FCSTD DOCUMENT  (FreeCAD 1.0R39109 (Git))
Label: Setup transmission
License: All rights reserved
LicenseURL: https://en.wikipedia.org/wiki/All_rights_reserved
objects: App::Link×30, PartDesign::CoordinateSystem×15, Part::FeaturePython×12, App::DocumentObjectGroup×2, App::FeaturePython×1, App::Part×1
note: 27 computed .brp shape members not serialized (recipe doc carries the construction recipe); baked Part::Feature solids carry a one-line shape summary decoded from their .brp
EXTERNAL_REF file=Optomecanics/Optical_table.FCStd obj=HoleAxis_1
EXTERNAL_REF file=Optomecanics/Optical_table.FCStd obj=Assembly
EXTERNAL_REF file=Cryostat/Cryo_sketch.FCStd obj=LCS_Origin
EXTERNAL_REF file=Cryostat/Cryo_sketch.FCStd obj=Assembly
EXTERNAL_REF file=Cryostat/Cryo_sketch.FCStd obj=Sample_position
EXTERNAL_REF file=Samples/Sample.FCStd obj=LCS_Origin
EXTERNAL_REF file=Samples/Sample.FCStd obj=Assembly
EXTERNAL_REF file=Optomecanics/Mount_assembly_1inch.FCStd obj=Botto_center_minus_6
EXTERNAL_REF file=Optomecanics/Mount_assembly_1inch.FCStd obj=Assembly
EXTERNAL_REF file=Optomecanics/Mount_assembly_1inch.FCStd obj=Bottom_center_6
EXTERNAL_REF file=Optomecanics/Mount_assembly_1inch.FCStd obj=Bottom_center_minus_20
EXTERNAL_REF file=Fiber components/Fiber_mount_assembly.FCStd obj=Center_minus_6deg
EXTERNAL_REF file=Fiber components/Fiber_mount_assembly.FCStd obj=Assembly
EXTERNAL_REF file=Fiber components/Fiber_mount_assembly.FCStd obj=Center_6deg
EXTERNAL_REF file=Optics/Mirror_1inch.FCStd obj=Mirror_face_center
EXTERNAL_REF file=Optomecanics/Mount_assembly_1inch.FCStd obj=LCS_3
EXTERNAL_REF file=Optics/Mirror_1inch.FCStd obj=BB1_E03_mirror
EXTERNAL_REF file=Fiber components/Fiber_mount_assembly.FCStd obj=Center_40det
EXTERNAL_REF file=Optomecanics/Mount_assembly_2inches.FCStd obj=LCS_Origin
EXTERNAL_REF file=Optomecanics/Mount_assembly_2inches.FCStd obj=Assembly
EXTERNAL_REF file=Optomecanics/Optical_table.FCStd obj=HoleAxis_14
EXTERNAL_REF file=Optomecanics/Mount_assembly_1inch.FCStd obj=Bottom_center
EXTERNAL_REF file=Optomecanics/Optical_table.FCStd obj=HoleAxis_15
EXTERNAL_REF file=Optomecanics/Mount_assembly_1inch.FCStd obj=Bottom_center_67
EXTERNAL_REF file=Optomecanics/Optical_table.FCStd obj=HoleAxis_12
EXTERNAL_REF file=Optomecanics/Optical_table.FCStd obj=HoleAxis_6
EXTERNAL_REF file=Optics/Monochromator.FCStd obj=LCS_1
EXTERNAL_REF file=Optics/Monochromator.FCStd obj=Assembly
EXTERNAL_REF file=Optomecanics/Mount_assembly_1inch.FCStd obj=_5
EXTERNAL_REF file=Optomecanics/Optical_table.FCStd obj=HoleAxis_7
EXTERNAL_REF file=Optomecanics/Optical_table.FCStd obj=HoleAxis_2
EXTERNAL_REF file=Optomecanics/Mount_assembly_1inch.FCStd obj=LCS_Origin
EXTERNAL_REF file=Optomecanics/Optical_table.FCStd obj=HoleAxis_17
EXTERNAL_REF file=Optics/Shamrock.FCStd obj=LCS_1
EXTERNAL_REF file=Optics/Shamrock.FCStd obj=Assembly

FEATURE [PartDesign::CoordinateSystem] LCS_Origin
  AttacherType = Attacher::AttachEngine3D
  AttachmentSupport = -> [X_Axis]
  MapMode = 2
FEATURE [App::DocumentObjectGroup] Constraints
FEATURE [App::FeaturePython] Variables  # WARN: FeaturePython — macro-defined, semantics opaque (R4)
  Type = App::PropertyContainer
FEATURE [App::DocumentObjectGroup] Configurations
FEATURE [PartDesign::CoordinateSystem] COLBERT_mirror_LCS  label="COLBERT_InputLensLCS"
  AttacherType = Attacher::AttachEngine3D
  Placement = pos=(0,400,0) rot=(0,0,1;0rad)
FEATURE [PartDesign::CoordinateSystem] Input_lens_LCS  label="ReflectedLensLCS"
  AttacherType = Attacher::AttachEngine3D
  Placement = pos=(26.13,248.63,0) rot=(0,0,1;0rad)
FEATURE [PartDesign::CoordinateSystem] Output_lens_LCS  label="InputLensLCS"
  AttacherType = Attacher::AttachEngine3D
  Placement = pos=(-26.13,248.63,0) rot=(0,0,1;0rad)
FEATURE [PartDesign::CoordinateSystem] Transmitted_lens_LCS  label="TransmittedLensLCS"
  AttacherType = Attacher::AttachEngine3D
  Placement = pos=(-26.13,-248.63,0) rot=(0,0,1;0rad)
FEATURE [PartDesign::CoordinateSystem] BS_LCS  label="BSLCS"
  AttacherType = Attacher::AttachEngine3D
  Placement = pos=(31.36,298.35,0) rot=(0,0,1;0rad)
FEATURE [PartDesign::CoordinateSystem] R_col_LCS  label="ReferenceColLCS"
  AttacherType = Attacher::AttachEngine3D
  Placement = pos=(-69,400,0) rot=(0,0,1;0rad)
FEATURE [PartDesign::CoordinateSystem] Reflection_col_LCS  label="ReflectionColLCS"
  AttacherType = Attacher::AttachEngine3D
  Placement = pos=(-31.36,298.36,0) rot=(0,0,1;0rad)
FEATURE [PartDesign::CoordinateSystem] Transmission_col_LCS  label="TransmissionColLCS"
  AttacherType = Attacher::AttachEngine3D
  Placement = pos=(-32.4,-308.3,0) rot=(0,0,1;0rad)
FEATURE [Part::FeaturePython] Ray003  label="Reference_beam"  # WARN: FeaturePython — macro-defined, semantics opaque (R4)
  BeamDistance = 0.1
  BeamNrColumns = 1
  BeamNrRows = 1
  ConeAngle = 360
  FocalPoint = (0,0,100)
  HideFirstPart = false
  MaxNrReflections = 200
  MaxRayLength = 170
  Order = 0
  Placement = pos=(41.81,397.81,199.9) rot=(0,0,-1;1.67552rad)
  Power = true
  RayBundleType = 0
  Spherical = false
  Wavelength = 580
FEATURE [App::Link] Optical_table
  AttachedBy = #HoleAxis_1
  AttachedTo = Parent Assembly#LCS_Origin
  LinkPlacement = pos=(546.1,-850.9,-110) rot=(0.57735,0.57735,0.57735;2.0944rad)
  LinkedObject = -> <external Optomecanics/Optical_table.FCStd>#Assembly
  Placement = pos=(546.1,-850.9,-110) rot=(0.57735,0.57735,0.57735;2.0944rad)
  SolverId = Asm4EE
  expr: Placement = LCS_Origin.Placement * AttachmentOffset * Optical_table#HoleAxis_1.Placement ^ -1
FEATURE [App::Link] Cryo
  AttachedBy = #LCS_Origin
  AttachedTo = Optical_table#HoleAxis_1
  LinkPlacement = pos=(-1.137e-13,1.137e-13,-1.279e-13) rot=(0,0,1;0rad)
  LinkedObject = -> <external Cryostat/Cryo_sketch.FCStd>#Assembly
  Placement = pos=(-1.137e-13,1.137e-13,-1.279e-13) rot=(0,0,1;0rad)
  SolverId = Asm4EE
  expr: Placement = Optical_table.Placement * Optical_table#HoleAxis_1.Placement * AttachmentOffset * Cryo_sketch#LCS_Origin.Placement ^ -1
FEATURE [App::Link] Sample
  AttachedBy = #LCS_Origin
  AttachedTo = Cryo#Sample_position
  LinkPlacement = pos=(-1.336e-13,1.236e-13,179.46) rot=(0,0,1;3.14159rad)
  LinkedObject = -> <external Samples/Sample.FCStd>#Assembly
  Placement = pos=(-1.336e-13,1.236e-13,179.46) rot=(0,0,1;3.14159rad)
  SolverId = Asm4EE
  expr: Placement = Cryo.Placement * Cryo_sketch#Sample_position.Placement * AttachmentOffset * Sample#LCS_Origin.Placement ^ -1
FEATURE [App::Link] Mount_assembly_1inch  label="InputLensMount"
  AttachedBy = #Botto_center_minus_6
  AttachedTo = Parent Assembly#Output_lens_LCS
  AttachmentOffset = pos=(0,0,0) rot=(0,0,1;1.5708rad)
  LinkPlacement = pos=(-26.13,248.63,0) rot=(0,0,1;1.67552rad)
  LinkedObject = -> <external Optomecanics/Mount_assembly_1inch.FCStd>#Assembly
  Placement = pos=(-26.13,248.63,0) rot=(0,0,1;1.67552rad)
  SolverId = Asm4EE
  expr: Placement = Output_lens_LCS.Placement * AttachmentOffset * Mount_assembly_1inch#Botto_center_minus_6.Placement ^ -1
FEATURE [App::Link] InputLensMount  label="ReflectedLensMount"
  AttachedBy = #Bottom_center_6
  AttachedTo = Parent Assembly#Input_lens_LCS
  AttachmentOffset = pos=(0,0,0) rot=(0,0,1;1.5708rad)
  LinkPlacement = pos=(26.13,248.63,0) rot=(0,0,1;1.46608rad)
  LinkedObject = -> <external Optomecanics/Mount_assembly_1inch.FCStd>#Assembly
  Placement = pos=(26.13,248.63,0) rot=(0,0,1;1.46608rad)
  SolverId = Asm4EE
  expr: Placement = Input_lens_LCS.Placement * AttachmentOffset * Mount_assembly_1inch#Bottom_center_6.Placement ^ -1
FEATURE [App::Link] Mount_assembly_1inch001  label="TransmittedLensMount"
  AttachedBy = #Botto_center_minus_6
  AttachedTo = Parent Assembly#Transmitted_lens_LCS
  AttachmentOffset = pos=(0,0,0) rot=(0,0,1;1.5708rad)
  LinkPlacement = pos=(-26.13,-248.63,0) rot=(0,0,1;1.67552rad)
  LinkedObject = -> <external Optomecanics/Mount_assembly_1inch.FCStd>#Assembly
  Placement = pos=(-26.13,-248.63,0) rot=(0,0,1;1.67552rad)
  SolverId = Asm4EE
  expr: Placement = Transmitted_lens_LCS.Placement * AttachmentOffset * Mount_assembly_1inch#Botto_center_minus_6.Placement ^ -1
FEATURE [App::Link] Mount_assembly_1inch002  label="BSMount"
  AttachedBy = #Bottom_center_minus_20
  AttachedTo = Parent Assembly#BS_LCS
  AttachmentOffset = pos=(0,0,0) rot=(0,0,1;4.71239rad)
  LinkPlacement = pos=(31.36,298.35,0) rot=(0,0,1;5.06145rad)
  LinkedObject = -> <external Optomecanics/Mount_assembly_1inch.FCStd>#Assembly
  Placement = pos=(31.36,298.35,0) rot=(0,0,1;5.06145rad)
  SolverId = Asm4EE
  expr: Placement = BS_LCS.Placement * AttachmentOffset * Mount_assembly_1inch#Bottom_center_minus_20.Placement ^ -1
FEATURE [App::Link] Fiber_mount_assembly  label="ReflectedFiberCol"
  AttachedBy = #Center_minus_6deg
  AttachedTo = Parent Assembly#Reflection_col_LCS
  AttachmentOffset = pos=(0,0,0) rot=(0,0,1;1.5708rad)
  LinkPlacement = pos=(-31.36,298.36,0) rot=(0,0,1;1.67552rad)
  LinkedObject = -> <external Fiber components/Fiber_mount_assembly.FCStd>#Assembly
  Placement = pos=(-31.36,298.36,0) rot=(0,0,1;1.67552rad)
  SolverId = Asm4EE
  expr: Placement = Reflection_col_LCS.Placement * AttachmentOffset * Fiber_mount_assembly#Center_minus_6deg.Placement ^ -1
FEATURE [App::Link] ReflectedFiberCol  label="TransmittedFiberCol"
  AttachedBy = #Center_6deg
  AttachedTo = Parent Assembly#Transmission_col_LCS
  AttachmentOffset = pos=(0,0,0) rot=(0,0,1;4.71239rad)
  LinkPlacement = pos=(-32.4,-308.3,0) rot=(0,0,1;4.60767rad)
  LinkedObject = -> <external Fiber components/Fiber_mount_assembly.FCStd>#Assembly
  Placement = pos=(-32.4,-308.3,0) rot=(0,0,1;4.60767rad)
  SolverId = Asm4EE
  expr: Placement = Transmission_col_LCS.Placement * AttachmentOffset * Fiber_mount_assembly#Center_6deg.Placement ^ -1
FEATURE [App::Link] BB1_E03_mirror  label="BS(Actually_a_mirror)"
  AttachedBy = #Mirror_face_center
  AttachedTo = Mount_assembly_1inch002#LCS_3
  AttachmentOffset = pos=(-4,0,0) rot=(0,0.707107,0.707107;3.14159rad)
  LinkPlacement = pos=(-5.01782,297.683,189.089) rot=(0,0,-1;2.79253rad)
  LinkedObject = -> <external Optics/Mirror_1inch.FCStd>#BB1_E03_mirror
  Placement = pos=(-5.01782,297.683,189.089) rot=(0,0,-1;2.79253rad)
  SolverId = Asm4EE
  expr: Placement = Mount_assembly_1inch002.Placement * Mount_assembly_1inch#LCS_3.Placement * AttachmentOffset * Mirror_1inch#Mirror_face_center.Placement ^ -1
FEATURE [Part::FeaturePython] Mirror  label="BS_Reflectance"  # WARN: FeaturePython — macro-defined, semantics opaque (R4)
  Base = -> [BB1_E03_mirror]
  OpticalType = 0
  Transparency = 0
  collectStatistics = false
FEATURE [Part::FeaturePython] Ray  label="Reflected_beam"  # WARN: FeaturePython — macro-defined, semantics opaque (R4)
  BeamDistance = 0.1
  BeamNrColumns = 1
  BeamNrRows = 1
  ConeAngle = 380
  FocalPoint = (0,0,100)
  HideFirstPart = false
  IgnoredOpticalElements = -> [Mirror]
  MaxNrReflections = 200
  MaxRayLength = 360
  Order = 0
  Placement = pos=(31.36,298.36,199.9) rot=(0,0,-1;1.67552rad)
  Power = true
  RayBundleType = 0
  Spherical = false
  Wavelength = 580
FEATURE [Part::FeaturePython] Mirror001  label="Sample_Reflectance"  # WARN: FeaturePython — macro-defined, semantics opaque (R4)
  Base = -> [Sample]
  OpticalType = 0
  Transparency = 0
  collectStatistics = false
FEATURE [Part::FeaturePython] Ray004  label="Transmitted_beam"  # WARN: FeaturePython — macro-defined, semantics opaque (R4)
  BeamDistance = 0.1
  BeamNrColumns = 1
  BeamNrRows = 1
  ConeAngle = 360
  FocalPoint = (0,0,100)
  HideFirstPart = false
  IgnoredOpticalElements = -> [Mirror,Mirror001]
  MaxNrReflections = 200
  MaxRayLength = 755
  Order = 0
  Placement = pos=(41.81,398.81,199.9) rot=(0,0,-1;1.67552rad)
  Power = true
  RayBundleType = 0
  Spherical = false
  Wavelength = 580
FEATURE [Part::FeaturePython] Ray005  label="COLBERT_beam"  # WARN: FeaturePython — macro-defined, semantics opaque (R4)
  BeamDistance = 12.7
  BeamNrColumns = 2
  BeamNrRows = 2
  ConeAngle = 360
  FocalPoint = (0,0,100)
  HideFirstPart = false
  IgnoredOpticalElements = -> [Mirror001]
  MaxNrReflections = 200
  MaxRayLength = 2000
  Order = 0
  Placement = pos=(-6.35,700,193.55) rot=(0,0,-1;1.5708rad)
  Power = true
  RayBundleType = 0
  Spherical = false
  Wavelength = 580
FEATURE [App::Link] Fiber_mount_assembly001  label="ReferenceFiberCol"
  AttachedBy = #Center_40det
  AttachedTo = Parent Assembly#R_col_LCS
  AttachmentOffset = pos=(0,0,0) rot=(0,0,1;3.14159rad)
  LinkPlacement = pos=(-69,400,0) rot=(0,0,1;2.3911rad)
  LinkedObject = -> <external Fiber components/Fiber_mount_assembly.FCStd>#Assembly
  Placement = pos=(-69,400,0) rot=(0,0,1;2.3911rad)
  SolverId = Asm4EE
  expr: Placement = R_col_LCS.Placement * AttachmentOffset * Fiber_mount_assembly#Center_40det.Placement ^ -1
FEATURE [App::Link] Mount_assembly_2inches  label="InputLensMountCOLBERT"
  AttachedBy = #LCS_Origin
  AttachedTo = Parent Assembly#COLBERT_mirror_LCS
  AttachmentOffset = pos=(0,100,0) rot=(0,0,1;1.5708rad)
  LinkPlacement = pos=(0,500,0) rot=(0,0,1;1.5708rad)
  LinkedObject = -> <external Optomecanics/Mount_assembly_2inches.FCStd>#Assembly
  Placement = pos=(0,500,0) rot=(0,0,1;1.5708rad)
  SolverId = Asm4EE
  expr: Placement = COLBERT_mirror_LCS.Placement * AttachmentOffset * Mount_assembly_2inches#LCS_Origin.Placement ^ -1
FEATURE [App::Link] Mount_assembly_2inches_2  label="OutputLensMountCOLBERT"
  AttachedBy = #LCS_Origin
  AttachedTo = Optical_table#HoleAxis_14
  AttachmentOffset = pos=(0,0,0) rot=(0,0,1;1.5708rad)
  LinkPlacement = pos=(-2.274e-13,-508,-9.95e-14) rot=(0,0,1;1.5708rad)
  LinkedObject = -> <external Optomecanics/Mount_assembly_2inches.FCStd>#Assembly
  Placement = pos=(-2.274e-13,-508,-9.95e-14) rot=(0,0,1;1.5708rad)
  SolverId = Asm4EE
  expr: Placement = Optical_table.Placement * Optical_table#HoleAxis_14.Placement * AttachmentOffset * Mount_assembly_2inches#LCS_Origin.Placement ^ -1
FEATURE [App::Link] Mount_assembly_1inch003  label="TransmissionMirror1MountCOLBERT"
  AttachedBy = #Bottom_center
  AttachedTo = Optical_table#HoleAxis_15
  AttachmentOffset = pos=(0,0,0) rot=(0,0,-1;4.71239rad)
  LinkPlacement = pos=(-3.411e-13,-609.6,-9.95e-14) rot=(0,0,-1;2.04203rad)
  LinkedObject = -> <external Optomecanics/Mount_assembly_1inch.FCStd>#Assembly
  Placement = pos=(-3.411e-13,-609.6,-9.95e-14) rot=(0,0,-1;2.04203rad)
  SolverId = Asm4EE
  expr: Placement = Optical_table.Placement * Optical_table#HoleAxis_15.Placement * AttachmentOffset * Mount_assembly_1inch#Bottom_center.Placement ^ -1
FEATURE [App::Link] Mount_assembly_1inch004  label="TransmissionMirror2MountCOLBERT"
  AttachedBy = #Bottom_center_67
  AttachedTo = Optical_table#HoleAxis_12
  AttachmentOffset = pos=(25.4,0,0) rot=(0,0,-1;1.5708rad)
  LinkPlacement = pos=(203.2,-457.2,-9.67e-14) rot=(0,0,-1;2.82743rad)
  LinkedObject = -> <external Optomecanics/Mount_assembly_1inch.FCStd>#Assembly
  Placement = pos=(203.2,-457.2,-9.67e-14) rot=(0,0,-1;2.82743rad)
  SolverId = Asm4EE
  expr: Placement = Optical_table.Placement * Optical_table#HoleAxis_12.Placement * AttachmentOffset * Mount_assembly_1inch#Bottom_center_67.Placement ^ -1
FEATURE [App::Link] Mount_assembly_2inches002  label="FinalLensMountCOLBERT"
  AttachedBy = #LCS_Origin
  AttachedTo = Optical_table#HoleAxis_6
  LinkPlacement = pos=(-101.6,-457.2,-1.279e-13) rot=(0,0,1;0rad)
  LinkedObject = -> <external Optomecanics/Mount_assembly_2inches.FCStd>#Assembly
  Placement = pos=(-101.6,-457.2,-1.279e-13) rot=(0,0,1;0rad)
  SolverId = Asm4EE
  expr: Placement = Optical_table.Placement * Optical_table#HoleAxis_6.Placement * AttachmentOffset * Mount_assembly_2inches#LCS_Origin.Placement ^ -1
FEATURE [App::Link] BB1_E03_mirror001  label="TransmissionMirror1COLBERT"
  AttachedBy = #Mirror_face_center
  AttachedTo = Mount_assembly_1inch003#LCS_3
  AttachmentOffset = pos=(-2,0,0) rot=(0,0.707107,0.707107;3.14159rad)
  LinkPlacement = pos=(-26.2053,-585.232,189.089) rot=(0,0,1;2.67035rad)
  LinkedObject = -> <external Optics/Mirror_1inch.FCStd>#BB1_E03_mirror
  Placement = pos=(-26.2053,-585.232,189.089) rot=(0,0,1;2.67035rad)
  SolverId = Asm4EE
  expr: Placement = Mount_assembly_1inch003.Placement * Mount_assembly_1inch#LCS_3.Placement * AttachmentOffset * Mirror_1inch#Mirror_face_center.Placement ^ -1
FEATURE [Part::FeaturePython] Mirror002  label="COLBERTTransmissionMirror1"  # WARN: FeaturePython — macro-defined, semantics opaque (R4)
  Base = -> [BB1_E03_mirror001]
  OpticalType = 0
  Transparency = 0
  collectStatistics = false
FEATURE [App::Link] BB1_E03_mirror002  label="TransmissionMirror2COLBERT"
  AttachedBy = #Mirror_face_center
  AttachedTo = Mount_assembly_1inch004#LCS_3
  AttachmentOffset = pos=(-3,0,0) rot=(0,-0.707107,0.707107;3.14159rad)
  LinkPlacement = pos=(224.12,-486.586,210.711) rot=(-0.809017,0.587785,0;3.14159rad)
  LinkedObject = -> <external Optics/Mirror_1inch.FCStd>#BB1_E03_mirror
  Placement = pos=(224.12,-486.586,210.711) rot=(-0.809017,0.587785,0;3.14159rad)
  SolverId = Asm4EE
  expr: Placement = Mount_assembly_1inch004.Placement * Mount_assembly_1inch#LCS_3.Placement * AttachmentOffset * Mirror_1inch#Mirror_face_center.Placement ^ -1
FEATURE [Part::FeaturePython] Mirror003  label="COLBERTTransmissionMirror2"  # WARN: FeaturePython — macro-defined, semantics opaque (R4)
  Base = -> [BB1_E03_mirror002]
  OpticalType = 0
  Transparency = 0
  collectStatistics = false
FEATURE [PartDesign::CoordinateSystem] InputCouplerLCS
  AttacherType = Attacher::AttachEngine3D
  Placement = pos=(37.63,358.03,0) rot=(0,0,1;0rad)
FEATURE [App::Link] Fiber_mount_assembly002  label="Fiber_mount_assembly"
  AttachedBy = #Center_6deg
  AttachedTo = Parent Assembly#InputCouplerLCS
  AttachmentOffset = pos=(0,0,0) rot=(0,0,1;1.5708rad)
  LinkPlacement = pos=(37.63,358.03,0) rot=(0,0,1;1.46608rad)
  LinkedObject = -> <external Fiber components/Fiber_mount_assembly.FCStd>#Assembly
  Placement = pos=(37.63,358.03,0) rot=(0,0,1;1.46608rad)
  SolverId = Asm4EE
  expr: Placement = InputCouplerLCS.Placement * AttachmentOffset * Fiber_mount_assembly#Center_6deg.Placement ^ -1
FEATURE [PartDesign::CoordinateSystem] MonochromatorLCS
  AttacherType = Attacher::AttachEngine3D
  Placement = pos=(330.2,-254,0) rot=(0,0,1;0rad)
FEATURE [App::Link] Monochromator
  AttachedBy = #LCS_1
  AttachedTo = Parent Assembly#MonochromatorLCS
  AttachmentOffset = pos=(15,10,0) rot=(0,0,1;3.14159rad)
  LinkPlacement = pos=(170.2,-344,0) rot=(0,0,1;3.14159rad)
  LinkedObject = -> <external Optics/Monochromator.FCStd>#Assembly
  Placement = pos=(170.2,-344,0) rot=(0,0,1;3.14159rad)
  SolverId = Asm4EE
  expr: Placement = MonochromatorLCS.Placement * AttachmentOffset * Monochromator#LCS_1.Placement ^ -1
FEATURE [PartDesign::CoordinateSystem] ReflectedLensReflectionConfigLCS
  AttacherType = Attacher::AttachEngine3D
  Placement = pos=(248.63,26.13,0) rot=(0,0,1;0rad)
FEATURE [App::Link] Mount_assembly_1inch005  label="ReflectionLensMountReflectionConfig"
  AttachedBy = #Botto_center_minus_6
  AttachedTo = Parent Assembly#ReflectedLensReflectionConfigLCS
  AttachmentOffset = pos=(0,2,0) rot=(0,0,1;0rad)
  LinkPlacement = pos=(248.63,28.13,0) rot=(0,0,1;0.10472rad)
  LinkedObject = -> <external Optomecanics/Mount_assembly_1inch.FCStd>#Assembly
  Placement = pos=(248.63,28.13,0) rot=(0,0,1;0.10472rad)
  SolverId = Asm4EE
  expr: Placement = ReflectedLensReflectionConfigLCS.Placement * AttachmentOffset * Mount_assembly_1inch#Botto_center_minus_6.Placement ^ -1
FEATURE [PartDesign::CoordinateSystem] LCS_1  label="ReflectedColReflectionConfigLCS"
  AttacherType = Attacher::AttachEngine3D
  Placement = pos=(298.35,31.36,0) rot=(0,0,1;0rad)
FEATURE [App::Link] Fiber_mount_assembly003  label="ReflectionColMountReflectionConfig"
  AttachedBy = #Center_minus_6deg
  AttachedTo = Parent Assembly#LCS_1
  AttachmentOffset = pos=(24,4.5,0) rot=(0,0,1;0rad)
  LinkPlacement = pos=(322.35,35.86,0) rot=(0,0,1;0.10472rad)
  LinkedObject = -> <external Fiber components/Fiber_mount_assembly.FCStd>#Assembly
  Placement = pos=(322.35,35.86,0) rot=(0,0,1;0.10472rad)
  SolverId = Asm4EE
  expr: Placement = LCS_1.Placement * AttachmentOffset * Fiber_mount_assembly#Center_minus_6deg.Placement ^ -1
FEATURE [App::Link] Mount_assembly_1inch006  label="ReflectionMirror1MountCOLBERT"
  AttachedBy = #_5
  AttachedTo = Optical_table#HoleAxis_7
  AttachmentOffset = pos=(0,5.5,0) rot=(0,0,1;1.5708rad)
  LinkPlacement = pos=(304.8,5.5,-9.98e-14) rot=(0,0,1;0.785398rad)
  LinkedObject = -> <external Optomecanics/Mount_assembly_1inch.FCStd>#Assembly
  Placement = pos=(304.8,5.5,-9.98e-14) rot=(0,0,1;0.785398rad)
  SolverId = Asm4EE
  expr: Placement = Optical_table.Placement * Optical_table#HoleAxis_7.Placement * AttachmentOffset * Mount_assembly_1inch#_5.Placement ^ -1
FEATURE [App::Link] Mount_assembly_1inch007  label="ReflectionMirror2MountCOLBERT"
  AttachedBy = #_5
  AttachedTo = Optical_table#HoleAxis_2
  LinkPlacement = pos=(304.8,-457.2,-8.53e-14) rot=(0,0,-1;0.785398rad)
  LinkedObject = -> <external Optomecanics/Mount_assembly_1inch.FCStd>#Assembly
  Placement = pos=(304.8,-457.2,-8.53e-14) rot=(0,0,-1;0.785398rad)
  SolverId = Asm4EE
  expr: Placement = Optical_table.Placement * Optical_table#HoleAxis_2.Placement * AttachmentOffset * Mount_assembly_1inch#_5.Placement ^ -1
FEATURE [App::Link] BB1_E03_mirror003  label="ReflectionMirror1COLBERT"
  AttachedBy = #Mirror_face_center
  AttachedTo = Mount_assembly_1inch006#LCS_3
  AttachmentOffset = pos=(-4,0,0) rot=(0,0.707107,0.707107;3.14159rad)
  LinkPlacement = pos=(320.778,-27.1877,189.089) rot=(0,0,1;5.49779rad)
  LinkedObject = -> <external Optics/Mirror_1inch.FCStd>#BB1_E03_mirror
  Placement = pos=(320.778,-27.1877,189.089) rot=(0,0,1;5.49779rad)
  SolverId = Asm4EE
  expr: Placement = Mount_assembly_1inch006.Placement * Mount_assembly_1inch#LCS_3.Placement * AttachmentOffset * Mirror_1inch#Mirror_face_center.Placement ^ -1
FEATURE [Part::FeaturePython] Mirror004  label="COLBERTReflectionMirror1"  # WARN: FeaturePython — macro-defined, semantics opaque (R4)
  Base = -> [BB1_E03_mirror003]
  OpticalType = 0
  Transparency = 0
  collectStatistics = false
FEATURE [App::Link] BB1_E03_mirror004  label="ReflectionMirror2COLBERT"
  AttachedBy = #Mirror_face_center
  AttachedTo = Mount_assembly_1inch007#LCS_3
  AttachmentOffset = pos=(-4,0,0) rot=(0,0.707107,0.707107;3.14159rad)
  LinkPlacement = pos=(272.112,-473.178,189.089) rot=(0,0,1;3.92699rad)
  LinkedObject = -> <external Optics/Mirror_1inch.FCStd>#BB1_E03_mirror
  Placement = pos=(272.112,-473.178,189.089) rot=(0,0,1;3.92699rad)
  SolverId = Asm4EE
  expr: Placement = Mount_assembly_1inch007.Placement * Mount_assembly_1inch#LCS_3.Placement * AttachmentOffset * Mirror_1inch#Mirror_face_center.Placement ^ -1
FEATURE [Part::FeaturePython] Mirror005  label="COLBERTReflectionMirror2"  # WARN: FeaturePython — macro-defined, semantics opaque (R4)
  Base = -> [BB1_E03_mirror004]
  OpticalType = 0
  Transparency = 0
  collectStatistics = false
FEATURE [App::Link] Mount_assembly_1inch008  label="ReflectionLensMountCOLBERT"
  AttachedBy = #LCS_Origin
  AttachedTo = Optical_table#HoleAxis_17
  AttachmentOffset = pos=(0,0,0) rot=(0,0,1;1.5708rad)
  LinkPlacement = pos=(304.8,-203.2,-9.95e-14) rot=(0,0,1;4.71239rad)
  LinkedObject = -> <external Optomecanics/Mount_assembly_1inch.FCStd>#Assembly
  Placement = pos=(304.8,-203.2,-9.95e-14) rot=(0,0,1;4.71239rad)
  SolverId = Asm4EE
  expr: Placement = Optical_table.Placement * Optical_table#HoleAxis_17.Placement * AttachmentOffset * Mount_assembly_1inch#LCS_Origin.Placement ^ -1
FEATURE [PartDesign::CoordinateSystem] FinalMirrorLCS
  AttacherType = Attacher::AttachEngine3D
  Placement = pos=(-152.4,-457.2,0) rot=(0,0,1;0rad)
FEATURE [PartDesign::CoordinateSystem] DetectorLCS  label="ShamrockLCS"
  AttacherType = Attacher::AttachEngine3D
  Placement = pos=(-152.4,-330.2,0) rot=(0,0,1;0rad)
FEATURE [App::Link] Mount_assembly_1inch009  label="FinalMirrorMountCOLBERT"
  AttachedBy = #_5
  AttachedTo = Parent Assembly#FinalMirrorLCS
  AttachmentOffset = pos=(0,-7,0) rot=(0,0,1;4.71239rad)
  LinkPlacement = pos=(-152.4,-464.2,0) rot=(0,0,1;3.92699rad)
  LinkedObject = -> <external Optomecanics/Mount_assembly_1inch.FCStd>#Assembly
  Placement = pos=(-152.4,-464.2,0) rot=(0,0,1;3.92699rad)
  SolverId = Asm4EE
  expr: Placement = FinalMirrorLCS.Placement * AttachmentOffset * Mount_assembly_1inch#_5.Placement ^ -1
FEATURE [App::Link] BB1_E03_mirror005  label="FinalMirrorCOLBERT"
  AttachedBy = #Mirror_face_center
  AttachedTo = Mount_assembly_1inch009#LCS_3
  AttachmentOffset = pos=(-4,0,0) rot=(0,0.707107,0.707107;3.14159rad)
  LinkPlacement = pos=(-168.378,-431.512,189.089) rot=(0,0,-1;3.92699rad)
  LinkedObject = -> <external Optics/Mirror_1inch.FCStd>#BB1_E03_mirror
  Placement = pos=(-168.378,-431.512,189.089) rot=(0,0,-1;3.92699rad)
  SolverId = Asm4EE
  expr: Placement = Mount_assembly_1inch009.Placement * Mount_assembly_1inch#LCS_3.Placement * AttachmentOffset * Mirror_1inch#Mirror_face_center.Placement ^ -1
FEATURE [Part::FeaturePython] Mirror006  label="COLBERTFinalMirror"  # WARN: FeaturePython — macro-defined, semantics opaque (R4)
  Base = -> [BB1_E03_mirror005]
  OpticalType = 0
  Transparency = 0
  collectStatistics = false
FEATURE [App::Link] Shamrock
  AttachedBy = #LCS_1
  AttachedTo = Parent Assembly#DetectorLCS
  LinkPlacement = pos=(-152.4,-279.4,0) rot=(0,0,-1;1.5708rad)
  LinkedObject = -> <external Optics/Shamrock.FCStd>#Assembly
  Placement = pos=(-152.4,-279.4,0) rot=(0,0,-1;1.5708rad)
  SolverId = Asm4EE
  expr: Placement = DetectorLCS.Placement * AttachmentOffset * Shamrock#LCS_1.Placement ^ -1
FEATURE [App::Part] Assembly
  AssemblyType = Part::Link
  Group = -> [LCS_Origin,Constraints,Variables,Configurations,COLBERT_mirror_LCS,Input_lens_LCS,Output_lens_LCS,Transmitted_lens_LCS,BS_LCS,R_col_LCS,Reflection_col_LCS,Transmission_col_LCS,InputCouplerLCS,MonochromatorLCS,ReflectedLensReflectionConfigLCS,LCS_1,FinalMirrorLCS,DetectorLCS,Optical_table,Cryo,Sample,Mount_assembly_1inch,InputLensMount,Mount_assembly_1inch001,Mount_assembly_1inch002,+23 more]
  Origin = -> Origin
  Type = Assembly
FEATURE [Part::FeaturePython] Absorber  label="ShamrockOptics"  # WARN: FeaturePython — macro-defined, semantics opaque (R4)
  Base = -> [Shamrock]
  OpticalType = 1
  Transparency = 0
  collectStatistics = false

RESOLVED EXTERNAL PARTS (link-assembly join: the EXTERNAL_REF files above that resolve inside this repo's crawl, each included once):
---- part Cryostat/Cryo_sketch.FCStd = doc fcstd_dc71c4d0d83d ----
FCSTD DOCUMENT  (FreeCAD 1.0R39109 (Git))
Label: Cryo_sketch
License: All rights reserved
LicenseURL: https://en.wikipedia.org/wiki/All_rights_reserved
objects: Sketcher::SketchObject×3, PartDesign::Hole×2, PartDesign::CoordinateSystem×2, App::DocumentObjectGroup×2, PartDesign::Pad×1, PartDesign::Body×1, App::FeaturePython×1, App::Part×1
note: 18 computed .brp shape members not serialized (recipe doc carries the construction recipe); baked Part::Feature solids carry a one-line shape summary decoded from their .brp

FEATURE [Sketcher::SketchObject] Sketch
  ArcFitTolerance = 0
  AttachmentSupport = -> [XY_Plane]
  FullyConstrained = true
  MakeInternals = false
  MapMode = 5
  sketch-geometry (1):
    g0: Circle CenterX=0 CenterY=0 CenterZ=0 NormalX=0 NormalY=0 NormalZ=1 AngleXU=0 Radius=162.5
  constraints (2):
    c: Coincident(g0,g-1)
    c: Diameter(g0) = 325
FEATURE [PartDesign::Pad] Pad
  Direction = (0,0,1)
  Length = 200
  Length2 = 10
  Profile = -> Sketch
  ReferenceAxis = -> Sketch [N_Axis]
  Suppressed = false
  Type = 0
FEATURE [Sketcher::SketchObject] Sketch001
  ArcFitTolerance = 0
  AttachmentOffset = pos=(0,0,175) rot=(0,0,1;0rad)
  AttachmentSupport = -> [YZ_Plane]
  FullyConstrained = true
  MakeInternals = false
  MapMode = 5
  Placement = pos=(175,0,0) rot=(0.57735,0.57735,0.57735;2.0944rad)
  sketch-geometry (1):
    g0: Circle CenterX=0 CenterY=199.9 CenterZ=0 NormalX=0 NormalY=0 NormalZ=1 AngleXU=0 Radius=20.44
  constraints (3):
    c: PointOnObject(g0,g-2)
    c: DistanceY(g-1,g0) = 199.9
    c: Diameter(g0) = 40.88
FEATURE [PartDesign::Hole] Hole
  BaseFeature = -> Pad
  CustomThreadClearance = 0
  Depth = 1123.84
  DepthType = 1
  Diameter = 40.88
  DrillForDepth = false
  DrillPoint = 1
  DrillPointAngle = 118
  HoleCutCountersinkAngle = 90
  HoleCutCustomValues = false
  HoleCutDepth = 0
  HoleCutDiameter = 6.1
  HoleCutType = 0
  ModelThread = false
  Profile = -> Sketch001
  Suppressed = false
  Tapered = false
  TaperedAngle = 90
  ThreadClass = 0
  ThreadDepth = 1123.84
  ThreadDepthType = 0
  ThreadDirection = 0
  ThreadFit = 0
  ThreadSize = 0
  ThreadType = 0
  Threaded = false
  UseCustomThreadClearance = false
FEATURE [Sketcher::SketchObject] Sketch002
  ArcFitTolerance = 0
  AttachmentOffset = pos=(0,0,175) rot=(0,0,1;0rad)
  AttachmentSupport = -> [XZ_Plane]
  FullyConstrained = true
  MakeInternals = false
  MapMode = 5
  Placement = pos=(0,-175,3.89e-14) rot=(1,0,0;1.5708rad)
  sketch-geometry (1):
    g0: Circle CenterX=0 CenterY=199.9 CenterZ=0 NormalX=0 NormalY=0 NormalZ=1 AngleXU=0 Radius=20.44
  constraints (3):
    c: PointOnObject(g0,g-2)
    c: DistanceY(g-1,g0) = 199.9
    c: Diameter(g0) = 40.88
FEATURE [PartDesign::Hole] Hole001
  BaseFeature = -> Hole
  CustomThreadClearance = 0
  Depth = 1045.89
  DepthType = 1
  Diameter = 40.88
  DrillForDepth = false
  DrillPoint = 1
  DrillPointAngle = 118
  HoleCutCountersinkAngle = 90
  HoleCutCustomValues = false
  HoleCutDepth = 0
  HoleCutDiameter = 0
  HoleCutType = 0
  ModelThread = false
  Profile = -> Sketch002
  Suppressed = false
  Tapered = false
  TaperedAngle = 90
  ThreadClass = 0
  ThreadDepth = 1045.89
  ThreadDepthType = 0
  ThreadDirection = 0
  ThreadFit = 0
  ThreadSize = 0
  ThreadType = 0
  Threaded = false
  UseCustomThreadClearance = false
FEATURE [PartDesign::Body] Body
  AllowCompound = false
  Group = -> [Sketch,Pad,Sketch001,Hole,Sketch002,Hole001]
  Origin = -> Origin
  Tip = -> Hole001
FEATURE [PartDesign::CoordinateSystem] LCS_Origin
  AttacherType = Attacher::AttachEngine3D
  AttachmentSupport = -> [X_Axis001]
  MapMode = 2
FEATURE [App::DocumentObjectGroup] Constraints
FEATURE [App::FeaturePython] Variables  # WARN: FeaturePython — macro-defined, semantics opaque (R4)
  Type = App::PropertyContainer
FEATURE [App::DocumentObjectGroup] Configurations
FEATURE [PartDesign::CoordinateSystem] Sample_position
  AttacherType = Attacher::AttachEngine3D
  Placement = pos=(0,0,179.46) rot=(0,0,1;3.14159rad)
FEATURE [App::Part] Assembly  label="Cryo"
  AssemblyType = Part::Link
  Group = -> [LCS_Origin,Constraints,Variables,Configurations,Body,Sample_position]
  Origin = -> Origin001
  Type = Assembly
---- part Optics/Monochromator.FCStd = doc fcstd_77c0743698dc ----
FCSTD DOCUMENT  (FreeCAD 1.0R39109 (Git))
Label: Monochromator
License: All rights reserved
LicenseURL: https://en.wikipedia.org/wiki/All_rights_reserved
objects: PartDesign::CoordinateSystem×2, App::DocumentObjectGroup×2, Sketcher::SketchObject×1, PartDesign::Pad×1, PartDesign::Body×1, App::FeaturePython×1, App::Part×1
note: 8 computed .brp shape members not serialized (recipe doc carries the construction recipe); baked Part::Feature solids carry a one-line shape summary decoded from their .brp

FEATURE [Sketcher::SketchObject] Sketch
  ArcFitTolerance = 1e-06
  AttachmentSupport = -> [XY_Plane]
  FullyConstrained = true
  MakeInternals = false
  MapMode = 5
  sketch-geometry (4):
    g0: LineSegment StartX=-175 StartY=90 StartZ=0 EndX=-175 EndY=-90 EndZ=0
    g1: LineSegment StartX=-175 StartY=-90 StartZ=0 EndX=175 EndY=-90 EndZ=0
    g2: LineSegment StartX=175 StartY=-90 StartZ=0 EndX=175 EndY=90 EndZ=0
    g3: LineSegment StartX=175 StartY=90 StartZ=0 EndX=-175 EndY=90 EndZ=0
  constraints (12):
    c: Coincident(g0,g1)
    c: Coincident(g1,g2)
    c: Coincident(g2,g3)
    c: Coincident(g3,g0)
    c: Vertical(g0)
    c: Vertical(g2)
    c: Horizontal(g1)
    c: Horizontal(g3)
    c: DistanceX(g3,g3) = 350
    c: DistanceY(g0,g0) = 180
    c: DistanceX(g0,g-1) = 175
    c: DistanceY(g-1,g2) = 90
FEATURE [PartDesign::Pad] Pad
  Direction = (0,0,1)
  Length = 125
  Length2 = 10
  Profile = -> Sketch
  ReferenceAxis = -> Sketch [N_Axis]
  Suppressed = false
  Type = 0
FEATURE [PartDesign::Body] Body
  AllowCompound = false
  Group = -> [Sketch,Pad]
  Origin = -> Origin
  Tip = -> Pad
FEATURE [PartDesign::CoordinateSystem] LCS_Origin
  AttacherType = Attacher::AttachEngine3D
  AttachmentSupport = -> [X_Axis001]
  MapMode = 2
FEATURE [App::DocumentObjectGroup] Constraints
FEATURE [App::FeaturePython] Variables  # WARN: FeaturePython — macro-defined, semantics opaque (R4)
  Type = App::PropertyContainer
FEATURE [App::DocumentObjectGroup] Configurations
FEATURE [PartDesign::CoordinateSystem] LCS_1  label="BottomCorner"
  AttacherType = Attacher::AttachEngine3D
  Placement = pos=(-175,-100,0) rot=(0,0,1;0rad)
FEATURE [App::Part] Assembly
  AssemblyType = Part::Link
  Group = -> [LCS_Origin,Constraints,Variables,Configurations,Body,LCS_1]
  Origin = -> Origin001
  Type = Assembly
---- part Optics/Shamrock.FCStd = doc fcstd_b0ad0143d256 ----
FCSTD DOCUMENT  (FreeCAD 1.0R39109 (Git))
Label: Shamrock
License: All rights reserved
LicenseURL: https://en.wikipedia.org/wiki/All_rights_reserved
objects: PartDesign::CoordinateSystem×2, App::DocumentObjectGroup×2, Sketcher::SketchObject×1, PartDesign::Pad×1, PartDesign::Body×1, App::FeaturePython×1, App::Part×1
note: 8 computed .brp shape members not serialized (recipe doc carries the construction recipe); baked Part::Feature solids carry a one-line shape summary decoded from their .brp

FEATURE [Sketcher::SketchObject] Sketch
  ArcFitTolerance = 1e-06
  AttachmentSupport = -> [XY_Plane]
  FullyConstrained = true
  MakeInternals = false
  MapMode = 5
  sketch-geometry (4):
    g0: LineSegment StartX=-50.8 StartY=38.1 StartZ=0 EndX=-50.8 EndY=-38.1 EndZ=0
    g1: LineSegment StartX=-50.8 StartY=-38.1 StartZ=0 EndX=50.8 EndY=-38.1 EndZ=0
    g2: LineSegment StartX=50.8 StartY=-38.1 StartZ=0 EndX=50.8 EndY=38.1 EndZ=0
    g3: LineSegment StartX=50.8 StartY=38.1 StartZ=0 EndX=-50.8 EndY=38.1 EndZ=0
  constraints (12):
    c: Coincident(g0,g1)
    c: Coincident(g1,g2)
    c: Coincident(g2,g3)
    c: Coincident(g3,g0)
    c: Vertical(g0)
    c: Vertical(g2)
    c: Horizontal(g1)
    c: Horizontal(g3)
    c: DistanceX(g3,g3) = 101.6
    c: DistanceY(g0,g0) = 76.2
    c: DistanceX(g0,g-1) = 50.8
    c: DistanceY(g-1,g2) = 38.1
FEATURE [PartDesign::Pad] Pad
  Direction = (0,0,1)
  Length = 250
  Length2 = 10
  Profile = -> Sketch
  ReferenceAxis = -> Sketch [N_Axis]
  Suppressed = false
  Type = 0
FEATURE [PartDesign::Body] Body
  AllowCompound = false
  Group = -> [Sketch,Pad]
  Origin = -> Origin
  Tip = -> Pad
FEATURE [PartDesign::CoordinateSystem] LCS_Origin
  AttacherType = Attacher::AttachEngine3D
  AttachmentSupport = -> [X_Axis001]
  MapMode = 2
FEATURE [App::DocumentObjectGroup] Constraints
FEATURE [App::FeaturePython] Variables  # WARN: FeaturePython — macro-defined, semantics opaque (R4)
  Type = App::PropertyContainer
FEATURE [App::DocumentObjectGroup] Configurations
FEATURE [PartDesign::CoordinateSystem] LCS_1
  AttacherType = Attacher::AttachEngine3D
  Placement = pos=(50.8,0,0) rot=(0,0,1;1.5708rad)
FEATURE [App::Part] Assembly
  AssemblyType = Part::Link
  Group = -> [LCS_Origin,Constraints,Variables,Configurations,Body,LCS_1]
  Origin = -> Origin001
  Type = Assembly
---- part Optomecanics/Mount_assembly_1inch.FCStd = doc fcstd_e10cc7f8b217 ----
FCSTD DOCUMENT  (FreeCAD 1.0R39109 (Git))
Label: Mount_assembly_1inch
License: All rights reserved
LicenseURL: https://en.wikipedia.org/wiki/All_rights_reserved
objects: PartDesign::CoordinateSystem×15, App::Link×3, App::DocumentObjectGroup×2, App::FeaturePython×1, App::Part×1
note: 15 computed .brp shape members not serialized (recipe doc carries the construction recipe); baked Part::Feature solids carry a one-line shape summary decoded from their .brp
EXTERNAL_REF file=Post_4inches.FCStd obj=HoleAxis_1
EXTERNAL_REF file=Post_4inches.FCStd obj=Assembly
EXTERNAL_REF file=PostSpacer_3inches.FCStd obj=HoleAxis_1
EXTERNAL_REF file=Post_4inches.FCStd obj=HoleAxis_2
EXTERNAL_REF file=PostSpacer_3inches.FCStd obj=Assembly
EXTERNAL_REF file=PostSpacer_3inches.FCStd obj=HoleAxis_2
EXTERNAL_REF file=lens_mount_1inch.FCStd obj=HoleAxis_1
EXTERNAL_REF file=lens_mount_1inch.FCStd obj=Assembly

FEATURE [PartDesign::CoordinateSystem] LCS_Origin
  AttacherType = Attacher::AttachEngine3D
  AttachmentSupport = -> [X_Axis]
  MapMode = 2
FEATURE [App::DocumentObjectGroup] Constraints
FEATURE [App::FeaturePython] Variables  # WARN: FeaturePython — macro-defined, semantics opaque (R4)
  Type = App::PropertyContainer
FEATURE [App::DocumentObjectGroup] Configurations
FEATURE [PartDesign::CoordinateSystem] Bottom_center_6
  AttacherType = Attacher::AttachEngine3D
  Placement = pos=(0,0,0) rot=(0,0,1;0.10472rad)
FEATURE [PartDesign::CoordinateSystem] LCS_3  label="Component_center"
  AttacherType = Attacher::AttachEngine3D
  Placement = pos=(0,0,199.9) rot=(0,0,1;0rad)
FEATURE [PartDesign::CoordinateSystem] Botto_center_minus_6  label="Bottom_center_minus_6"
  AttacherType = Attacher::AttachEngine3D
  Placement = pos=(0,0,0) rot=(0,0,-1;0.10472rad)
FEATURE [PartDesign::CoordinateSystem] _5  label="Bottom_center_45"
  AttacherType = Attacher::AttachEngine3D
  Placement = pos=(0,0,0) rot=(0,0,1;0.785398rad)
FEATURE [App::Link] Post_4inches
  AttachedBy = #HoleAxis_1
  AttachedTo = Parent Assembly#LCS_Origin
  LinkPlacement = pos=(-5.3e-15,-1.07e-14,50.8) rot=(0.57735,0.57735,0.57735;2.0944rad)
  LinkedObject = -> <external Post_4inches.FCStd>#Assembly
  Placement = pos=(-5.3e-15,-1.07e-14,50.8) rot=(0.57735,0.57735,0.57735;2.0944rad)
  SolverId = Asm4EE
  expr: Placement = LCS_Origin.Placement * AttachmentOffset * Post_4inches#HoleAxis_1.Placement ^ -1
FEATURE [App::Link] PostSpacer_3inches
  AttachedBy = #HoleAxis_1
  AttachedTo = Post_4inches#HoleAxis_2
  LinkPlacement = pos=(-1.39295,-15.1208,153.495) rot=(0.57735,0.57735,0.57735;2.0944rad)
  LinkedObject = -> <external PostSpacer_3inches.FCStd>#Assembly
  Placement = pos=(-1.39295,-15.1208,153.495) rot=(0.57735,0.57735,0.57735;2.0944rad)
  SolverId = Asm4EE
  expr: Placement = Post_4inches.Placement * Post_4inches#HoleAxis_2.Placement * AttachmentOffset * PostSpacer_3inches#HoleAxis_1.Placement ^ -1
FEATURE [App::Link] lens_mount_1inch
  AttachedBy = #HoleAxis_1
  AttachedTo = PostSpacer_3inches#HoleAxis_2
  AttachmentOffset = pos=(0,0,0) rot=(0,1,0;3.14159rad)
  LinkPlacement = pos=(-5.08,2.3e-14,199.898) rot=(-0.57735,0.57735,0.57735;4.18879rad)
  LinkedObject = -> <external lens_mount_1inch.FCStd>#Assembly
  Placement = pos=(-5.08,2.3e-14,199.898) rot=(-0.57735,0.57735,0.57735;4.18879rad)
  SolverId = Asm4EE
  expr: Placement = PostSpacer_3inches.Placement * PostSpacer_3inches#HoleAxis_2.Placement * AttachmentOffset * lens_mount_1inch#HoleAxis_1.Placement ^ -1
FEATURE [PartDesign::CoordinateSystem] Bottom_center_39
  AttacherType = Attacher::AttachEngine3D
  Placement = pos=(0,0,0) rot=(0,0,1;0.680678rad)
FEATURE [PartDesign::CoordinateSystem] Bottom_center_25  label="Bottom_center_16"
  AttacherType = Attacher::AttachEngine3D
  Placement = pos=(0,0,0) rot=(0,0,1;0.279253rad)
FEATURE [PartDesign::CoordinateSystem] Bottom_center_74  label="Bottom_center_65"
  AttacherType = Attacher::AttachEngine3D
  Placement = pos=(0,0,0) rot=(0,0,1;1.13446rad)
FEATURE [PartDesign::CoordinateSystem] Bottom_center_20
  AttacherType = Attacher::AttachEngine3D
  Placement = pos=(0,0,0) rot=(0,0,1;0.349066rad)
FEATURE [PartDesign::CoordinateSystem] Bottom_center_minus_20
  AttacherType = Attacher::AttachEngine3D
  Placement = pos=(0,0,0) rot=(0,0,-1;0.349066rad)
FEATURE [PartDesign::CoordinateSystem] Bottom_center_51
  AttacherType = Attacher::AttachEngine3D
  Placement = pos=(0,0,0) rot=(0,0,1;0.890118rad)
FEATURE [PartDesign::CoordinateSystem] Bottom_center_15
  AttacherType = Attacher::AttachEngine3D
  Placement = pos=(0,0,0) rot=(0,0,1;0.261799rad)
FEATURE [PartDesign::CoordinateSystem] Bottom_center_70  label="Bottom_center_55"
  AttacherType = Attacher::AttachEngine3D
  Placement = pos=(0,0,0) rot=(0,0,1;0.959931rad)
FEATURE [PartDesign::CoordinateSystem] Bottom_center  label="Bottom_center_27"
  AttacherType = Attacher::AttachEngine3D
  Placement = pos=(0,0,0) rot=(0,0,1;0.471239rad)
FEATURE [PartDesign::CoordinateSystem] Bottom_center_67  label="Bottom_center_72"
  AttacherType = Attacher::AttachEngine3D
  Placement = pos=(0,0,0) rot=(0,0,1;1.25664rad)
FEATURE [App::Part] Assembly
  AssemblyType = Part::Link
  Group = -> [LCS_Origin,Constraints,Variables,Configurations,Bottom_center_6,LCS_3,Botto_center_minus_6,_5,Post_4inches,PostSpacer_3inches,lens_mount_1inch,Bottom_center_39,Bottom_center_25,Bottom_center_74,Bottom_center_20,Bottom_center_minus_20,Bottom_center_51,Bottom_center_15,Bottom_center_70,Bottom_center,Bottom_center_67]
  Origin = -> Origin
  Type = Assembly
---- part Optomecanics/Mount_assembly_2inches.FCStd = doc fcstd_1b987de1cbfe ----
FCSTD DOCUMENT  (FreeCAD 1.0R39109 (Git))
Label: Mount_assembly_2inches
License: All rights reserved
LicenseURL: https://en.wikipedia.org/wiki/All_rights_reserved
objects: PartDesign::CoordinateSystem×4, App::Link×3, App::DocumentObjectGroup×2, App::FeaturePython×1, App::Part×1
note: 4 computed .brp shape members not serialized (recipe doc carries the construction recipe); baked Part::Feature solids carry a one-line shape summary decoded from their .brp
EXTERNAL_REF file=Post_6inches.FCStd obj=HoleAxis_1
EXTERNAL_REF file=Post_6inches.FCStd obj=Assembly
EXTERNAL_REF file=Buffer_2inchesOptics.FCStd obj=Bottom_center
EXTERNAL_REF file=Post_6inches.FCStd obj=HoleAxis_2
EXTERNAL_REF file=Buffer_2inchesOptics.FCStd obj=Assembly
EXTERNAL_REF file=Buffer_2inchesOptics.FCStd obj=Top_center
EXTERNAL_REF file=lens_mount_2inches.FCStd obj=HoleAxis_2
EXTERNAL_REF file=lens_mount_2inches.FCStd obj=Assembly

FEATURE [PartDesign::CoordinateSystem] LCS_Origin
  AttacherType = Attacher::AttachEngine3D
  AttachmentSupport = -> [X_Axis]
  MapMode = 2
FEATURE [App::DocumentObjectGroup] Constraints
FEATURE [App::FeaturePython] Variables  # WARN: FeaturePython — macro-defined, semantics opaque (R4)
  Type = App::PropertyContainer
FEATURE [App::DocumentObjectGroup] Configurations
FEATURE [App::Link] Post_6inches
  AttachedBy = #HoleAxis_1
  AttachedTo = Parent Assembly#LCS_Origin
  AttachmentOffset = pos=(0,0,0) rot=(0,1,0;3.14159rad)
  LinkPlacement = pos=(-9.3e-15,7.1e-15,76.2) rot=(-0.57735,0.57735,0.57735;4.18879rad)
  LinkedObject = -> <external Post_6inches.FCStd>#Assembly
  Placement = pos=(-9.3e-15,7.1e-15,76.2) rot=(-0.57735,0.57735,0.57735;4.18879rad)
  SolverId = Asm4EE
  expr: Placement = LCS_Origin.Placement * AttachmentOffset * Post_6inches#HoleAxis_1.Placement ^ -1
FEATURE [App::Link] Buffer_2inchesOptics
  AttachedBy = #Bottom_center
  AttachedTo = Post_6inches#HoleAxis_2
  LinkPlacement = pos=(-3.89e-14,1.35e-14,152.4) rot=(0,0,1;0rad)
  LinkedObject = -> <external Buffer_2inchesOptics.FCStd>#Assembly
  Placement = pos=(-3.89e-14,1.35e-14,152.4) rot=(0,0,1;0rad)
  SolverId = Asm4EE
  expr: Placement = Post_6inches.Placement * Post_6inches#HoleAxis_2.Placement * AttachmentOffset * Buffer_2inchesOptics#Bottom_center.Placement ^ -1
FEATURE [App::Link] lens_mount_2inches
  AttachedBy = #HoleAxis_2
  AttachedTo = Buffer_2inchesOptics#Top_center
  LinkPlacement = pos=(14.5044,-31.1596,232.238) rot=(-0.57735,0.57735,0.57735;4.18879rad)
  LinkedObject = -> <external lens_mount_2inches.FCStd>#Assembly
  Placement = pos=(14.5044,-31.1596,232.238) rot=(-0.57735,0.57735,0.57735;4.18879rad)
  SolverId = Asm4EE
  expr: Placement = Buffer_2inchesOptics.Placement * Buffer_2inchesOptics#Top_center.Placement * AttachmentOffset * lens_mount_2inches#HoleAxis_2.Placement ^ -1
FEATURE [PartDesign::CoordinateSystem] LCS_1  label="Center45"
  AttacherType = Attacher::AttachEngine3D
  Placement = pos=(0,0,0) rot=(0,0,1;0.785398rad)
FEATURE [PartDesign::CoordinateSystem] LCS_2  label="ComponentCenter"
  AttacherType = Attacher::AttachEngine3D
  Placement = pos=(0,0,199.9) rot=(0,0,1;0rad)
FEATURE [PartDesign::CoordinateSystem] Component_center_20  label="Component_center_55"
  AttacherType = Attacher::AttachEngine3D
  Placement = pos=(0,0,0) rot=(0,0,1;0.959931rad)
FEATURE [App::Part] Assembly
  AssemblyType = Part::Link
  Group = -> [LCS_Origin,Constraints,Variables,Configurations,Post_6inches,Buffer_2inchesOptics,lens_mount_2inches,LCS_1,LCS_2,Component_center_20]
  Origin = -> Origin
  Type = Assembly
---- part Samples/Sample.FCStd = doc fcstd_5ff7477491c1 ----
FCSTD DOCUMENT  (FreeCAD 1.0R39109 (Git))
Label: Sample
License: All rights reserved
LicenseURL: https://en.wikipedia.org/wiki/All_rights_reserved
objects: PartDesign::CoordinateSystem×2, App::DocumentObjectGroup×2, Sketcher::SketchObject×1, PartDesign::Pad×1, PartDesign::Body×1, App::FeaturePython×1, App::Part×1
note: 8 computed .brp shape members not serialized (recipe doc carries the construction recipe); baked Part::Feature solids carry a one-line shape summary decoded from their .brp

FEATURE [Sketcher::SketchObject] Sketch
  ArcFitTolerance = 0
  AttachmentSupport = -> [XY_Plane]
  FullyConstrained = true
  MakeInternals = false
  MapMode = 5
  sketch-geometry (4):
    g0: LineSegment StartX=-12.7 StartY=1.5825 StartZ=0 EndX=12.7 EndY=1.5825 EndZ=0
    g1: LineSegment StartX=12.7 StartY=1.5825 StartZ=0 EndX=12.7 EndY=-1.5875 EndZ=0
    g2: LineSegment StartX=12.7 StartY=-1.5875 StartZ=0 EndX=-12.7 EndY=-1.5875 EndZ=0
    g3: LineSegment StartX=-12.7 StartY=-1.5875 StartZ=0 EndX=-12.7 EndY=1.5825 EndZ=0
  constraints (12):
    c: Coincident(g0,g1)
    c: Coincident(g1,g2)
    c: Coincident(g2,g3)
    c: Coincident(g3,g0)
    c: Horizontal(g0)
    c: Horizontal(g2)
    c: Vertical(g1)
    c: Vertical(g3)
    c: DistanceX(g2,g2) = 25.4
    c: DistanceX(g-1,g1) = 12.7
    c: DistanceY(g1,g1) = -3.17
    c: DistanceY(g1,g-1) = 1.5875
FEATURE [PartDesign::Pad] Pad
  Direction = (0,0,1)
  Length = 30
  Length2 = 10
  Profile = -> Sketch
  ReferenceAxis = -> Sketch [N_Axis]
  Suppressed = false
  Type = 0
FEATURE [PartDesign::Body] Body
  AllowCompound = false
  Group = -> [Sketch,Pad]
  Origin = -> Origin
  Tip = -> Pad
FEATURE [PartDesign::CoordinateSystem] LCS_Origin
  AttacherType = Attacher::AttachEngine3D
  AttachmentSupport = -> [X_Axis001]
  MapMode = 2
FEATURE [App::DocumentObjectGroup] Constraints
FEATURE [App::FeaturePython] Variables  # WARN: FeaturePython — macro-defined, semantics opaque (R4)
  Type = App::PropertyContainer
FEATURE [App::DocumentObjectGroup] Configurations
FEATURE [PartDesign::CoordinateSystem] LCS_1  label="45_deg"
  AttacherType = Attacher::AttachEngine3D
  Placement = pos=(0,0,0) rot=(0,0,1;0.785398rad)
FEATURE [App::Part] Assembly  label="Sample"
  AssemblyType = Part::Link
  Group = -> [LCS_Origin,Constraints,Variables,Configurations,Body,LCS_1]
  Origin = -> Origin001
  Type = Assembly
